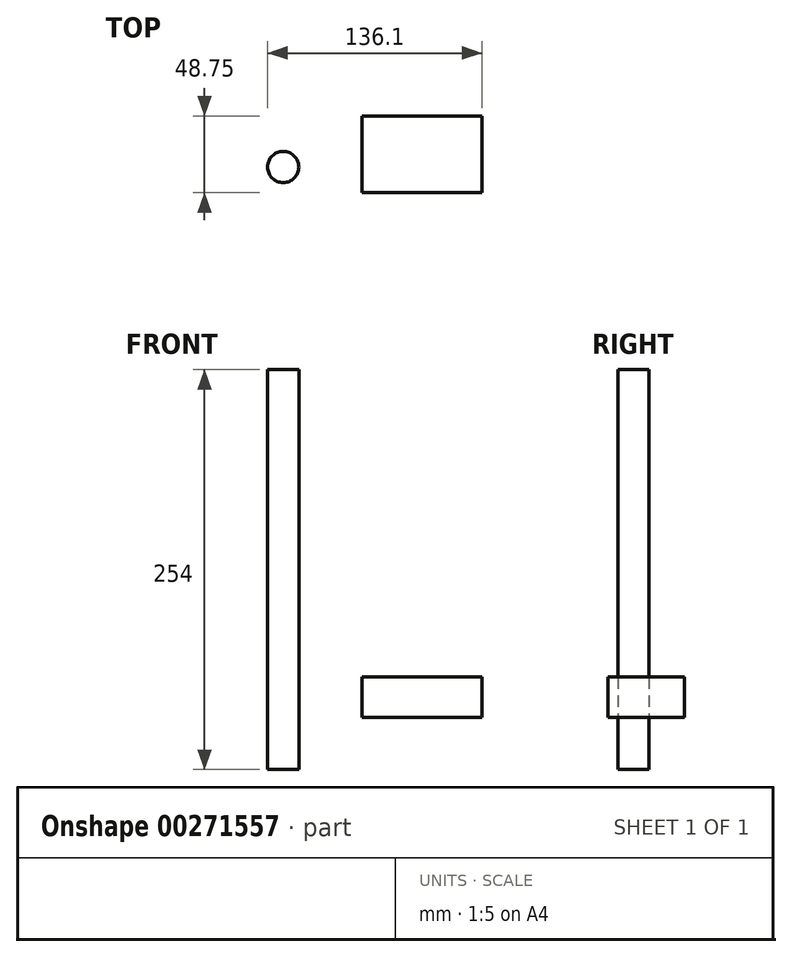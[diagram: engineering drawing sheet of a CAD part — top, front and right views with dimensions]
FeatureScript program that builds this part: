
annotation { "Feature Type Name" : "Feature", "Feature Type Description" : "" }
export const myFeature = defineFeature(function(context is Context, id is Id, definition is map)
    precondition{}
    {
        {
            var Q0;
            Q0=qCreatedBy(makeId("Top.planeOp"),FACE);
            var sketch = newSketch(context, id + "F0", { "sketchPlane" : qUnion([Q0])});
            skCircle(sketch, "E0", {"center": v(-49.98, -32.44) * mm, "radius": 9.92 * mm});
            skSolve(sketch);
        }
        {
            var Q0;
            Q0 = qSketchRegion(id + "F0", true);
            extrude(context, id + "F1", {"entities" : qUnion([Q0]), "depth" : 254 * mm});
        }
        {
            var Q0;
            Q0=qCreatedBy(makeId("Right.planeOp"),FACE);
            var sketch = newSketch(context, id + "F2", { "sketchPlane" : qUnion([Q0])});
            skLineSegment(sketch, "E1.bottom", {"start": v(-48.75, 58.8) * mm, "end": v(0, 58.8) * mm});
            skLineSegment(sketch, "E1.top", {"start": v(-48.75, 33.12) * mm, "end": v(0, 33.12) * mm});
            skLineSegment(sketch, "E1.left", {"start": v(-48.75, 58.8) * mm, "end": v(-48.75, 33.12) * mm});
            skLineSegment(sketch, "E1.right", {"start": v(0, 58.8) * mm, "end": v(0, 33.12) * mm});
            skSolve(sketch);
        }
        {
            var Q0;
            Q0 = qSketchRegion(id + "F2", true);
            extrude(context, id + "F3", {"entities" : qUnion([Q0]), "depth" : 76.2 * mm});
        }
    });
